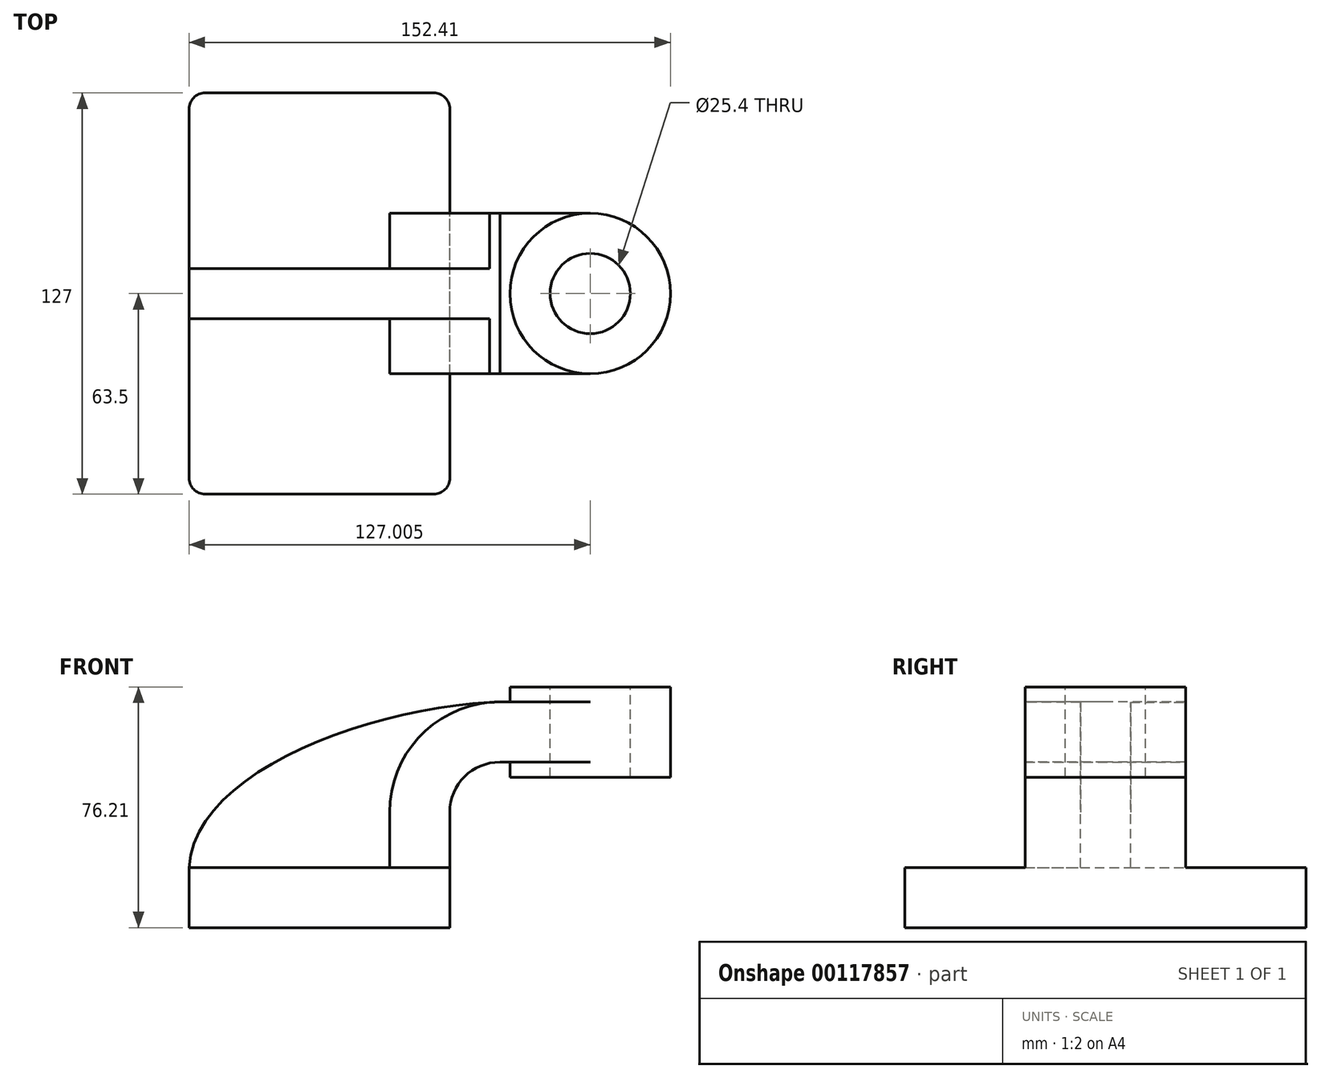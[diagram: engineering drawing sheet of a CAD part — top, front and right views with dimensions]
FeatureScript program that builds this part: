
annotation { "Feature Type Name" : "Feature", "Feature Type Description" : "" }
export const myFeature = defineFeature(function(context is Context, id is Id, definition is map)
    precondition{}
    {
        {
            var Q0;
            Q0=qCreatedBy(makeId("Front.planeOp"),FACE);
            var sketch = newSketch(context, id + "F0", { "sketchPlane" : qUnion([Q0])});
            skLineSegment(sketch, "E0.rect.bottom", {"start": v(-41.28, 9.52) * mm, "end": v(41.28, 9.52) * mm});
            skLineSegment(sketch, "E0.rect.top", {"start": v(-41.28, -9.52) * mm, "end": v(41.28, -9.52) * mm});
            skLineSegment(sketch, "E0.rect.left", {"start": v(-41.28, 9.52) * mm, "end": v(-41.28, -9.52) * mm});
            skLineSegment(sketch, "E0.rect.right", {"start": v(41.28, 9.52) * mm, "end": v(41.28, -9.52) * mm});
            skPoint(sketch, "E0.rect.middle", {"position": v(0, 0) * mm});
            skLineSegment(sketch, "E1", {"start": v(41.28, 9.52) * mm, "end": v(41.28, 27) * mm});
            skArc(sketch, "E2", {"start": v(41.28, 27) * mm, "mid": v(45.92, 38.23) * mm, "end": v(57.15, 42.88) * mm});
            skLineSegment(sketch, "E3", {"start": v(57.15, 42.88) * mm, "end": v(85.72, 42.88) * mm});
            skLineSegment(sketch, "E4.rect.bottom", {"start": v(60.32, 38.1) * mm, "end": v(111.12, 38.1) * mm});
            skLineSegment(sketch, "E4.rect.top", {"start": v(60.32, 66.68) * mm, "end": v(111.12, 66.68) * mm});
            skLineSegment(sketch, "E4.rect.left", {"start": v(60.32, 38.1) * mm, "end": v(60.32, 66.68) * mm});
            skLineSegment(sketch, "E4.rect.right", {"start": v(111.13, 38.1) * mm, "end": v(111.12, 66.68) * mm});
            skPoint(sketch, "E4.rect.middle", {"position": v(85.72, 52.39) * mm});
            skLineSegment(sketch, "E5.0", {"start": v(57.15, 61.93) * mm, "end": v(85.72, 61.93) * mm});
            skArc(sketch, "E5.1", {"start": v(22.23, 27) * mm, "mid": v(32.45, 51.7) * mm, "end": v(57.15, 61.93) * mm});
            skLineSegment(sketch, "E5.2", {"start": v(22.23, 9.52) * mm, "end": v(22.23, 27) * mm});
            skLineSegment(sketch, "E6", {"start": v(85.72, 38.1) * mm, "end": v(85.72, 66.68) * mm});
            skFitSpline(sketch, "E7", {"points": [v(-41.28, 9.53) * mm, v(57.15, 61.93) * mm], "startDerivative": vector(5.2, 92.34) * mm, "endDerivative": vector(120.92, 4.22) * mm});
            skSolve(sketch);
        }
        {
            var Q0;
            Q0=makeQuery(id+"F0.imprint","IMPRINT",FACE,{"disambiguationData":[TD([[makeQuery(id+"F0.imprint","IMPRINT",EDGE,{"derivedFrom":sQuery(id+"F0.wireOp",EDGE,"E0.rect.top")}),1.0]])]});
            extrude(context, id + "F1", {"entities" : qUnion([Q0]), "endBound" : BoundingType.SYMMETRIC, "depth" : 127 * mm});
        }
        {
            var Q0;
            {var subQ9=sQuery(id+"F0.wireOp",EDGE,"E1");Q0=makeQuery(id+"F0.imprint","IMPRINT",FACE,{"disambiguationData":[TD([[makeQuery(id+"F0.imprint","IMPRINT",EDGE,{"derivedFrom":subQ9}),1.0]])]});}
            var Q1;
            {var subQ0=sQuery(id+"F0.wireOp",EDGE,"E6");var subQ1=sQuery(id+"F0.wireOp",EDGE,"E3");var subQ2=makeQuery(id+"F0.imprint","INTERSECT",VERTEX,{"derivedFrom":[subQ1,subQ0]});Q1=makeQuery(id+"F0.imprint","IMPRINT",FACE,{"disambiguationData":[TD([[makeQuery(id+"F0.imprint","IMPRINT",EDGE,{"disambiguationData":[TD([[subQ2,1.0]])],"derivedFrom":subQ1}),1.0]])]});}
            extrude(context, id + "F2", {"entities" : qUnion([Q0, Q1]), "operationType" : NewBodyOperationType.ADD, "endBound" : BoundingType.SYMMETRIC, "depth" : 50.8 * mm});
        }
        {
            var Q0;
            {var subQ3=sQuery(id+"F0.wireOp",EDGE,"E5.2");Q0=makeQuery(id+"F0.imprint","IMPRINT",FACE,{"disambiguationData":[TD([[makeQuery(id+"F0.imprint","IMPRINT",EDGE,{"derivedFrom":subQ3}),1.0]])]});}
            extrude(context, id + "F3", {"entities" : qUnion([Q0]), "operationType" : NewBodyOperationType.ADD, "endBound" : BoundingType.SYMMETRIC, "depth" : 15.88 * mm});
        }
        {
            var Q0;
            {var subQ5=sQuery(id+"F0.wireOp",EDGE,"E4.rect.right");Q0=makeQuery(id+"F0.imprint","IMPRINT",FACE,{"disambiguationData":[TD([[makeQuery(id+"F0.imprint","IMPRINT",EDGE,{"derivedFrom":subQ5}),1.0]])]});}
            var Q1;
            Q1=sQuery(id+"F0.wireOp",EDGE,"E6");
            revolve(context, id + "F4", {"operationType" : NewBodyOperationType.ADD, "entities" : qUnion([Q0]), "axis" : qUnion([Q1]), "revolveType" : RevolveType.FULL});
        }
        {
            var Q0;
            Q0=makeQuery(id+"F1.opExtrude","CAP_EDGE",EDGE,{"disambiguationData":[OSD([sQuery(id+"F0.wireOp",EDGE,"E0.rect.right")])],"isStart":false});
            var Q1;
            Q1=makeQuery(id+"F1.opExtrude","CAP_EDGE",EDGE,{"disambiguationData":[OSD([sQuery(id+"F0.wireOp",EDGE,"E0.rect.left")])],"isStart":false});
            var Q2;
            Q2=makeQuery(id+"F1.opExtrude","CAP_EDGE",EDGE,{"disambiguationData":[OSD([sQuery(id+"F0.wireOp",EDGE,"E0.rect.right")])],"isStart":true});
            var Q3;
            Q3=makeQuery(id+"F1.opExtrude","CAP_EDGE",EDGE,{"disambiguationData":[OSD([sQuery(id+"F0.wireOp",EDGE,"E0.rect.left")])],"isStart":true});
            fillet(context, id + "F5", {"entities" : qUnion([Q0, Q1, Q2, Q3]), "radius" : 5.08 * mm, "tangentPropagation" : true, "allowEdgeOverflow" : false});
        }
        {
            var Q0;
            Q0=makeQuery(id+"F4.opRevolve","SWEPT_FACE",FACE,{"disambiguationData":[OSD([sQuery(id+"F0.wireOp",EDGE,"E4.rect.top")])]});
            var sketch = newSketch(context, id + "F6", { "sketchPlane" : qUnion([Q0])});
            skCircle(sketch, "E8", {"center": v(85.72, 0) * mm, "radius": 12.7 * mm});
            skSolve(sketch);
        }
        {
            var Q0;
            Q0=makeQuery(id+"F6.imprint","IMPRINT",FACE,{"disambiguationData":[TD([[makeQuery(id+"F6.imprint","IMPRINT",EDGE,{"derivedFrom":sQuery(id+"F6.wireOp",EDGE,"E8")}),1.0]])]});
            extrude(context, id + "F7", {"entities" : qUnion([Q0]), "operationType" : NewBodyOperationType.REMOVE, "endBound" : BoundingType.THROUGH_ALL, "oppositeDirection" : true, "depth" : 25.4 * mm});
        }
    });
